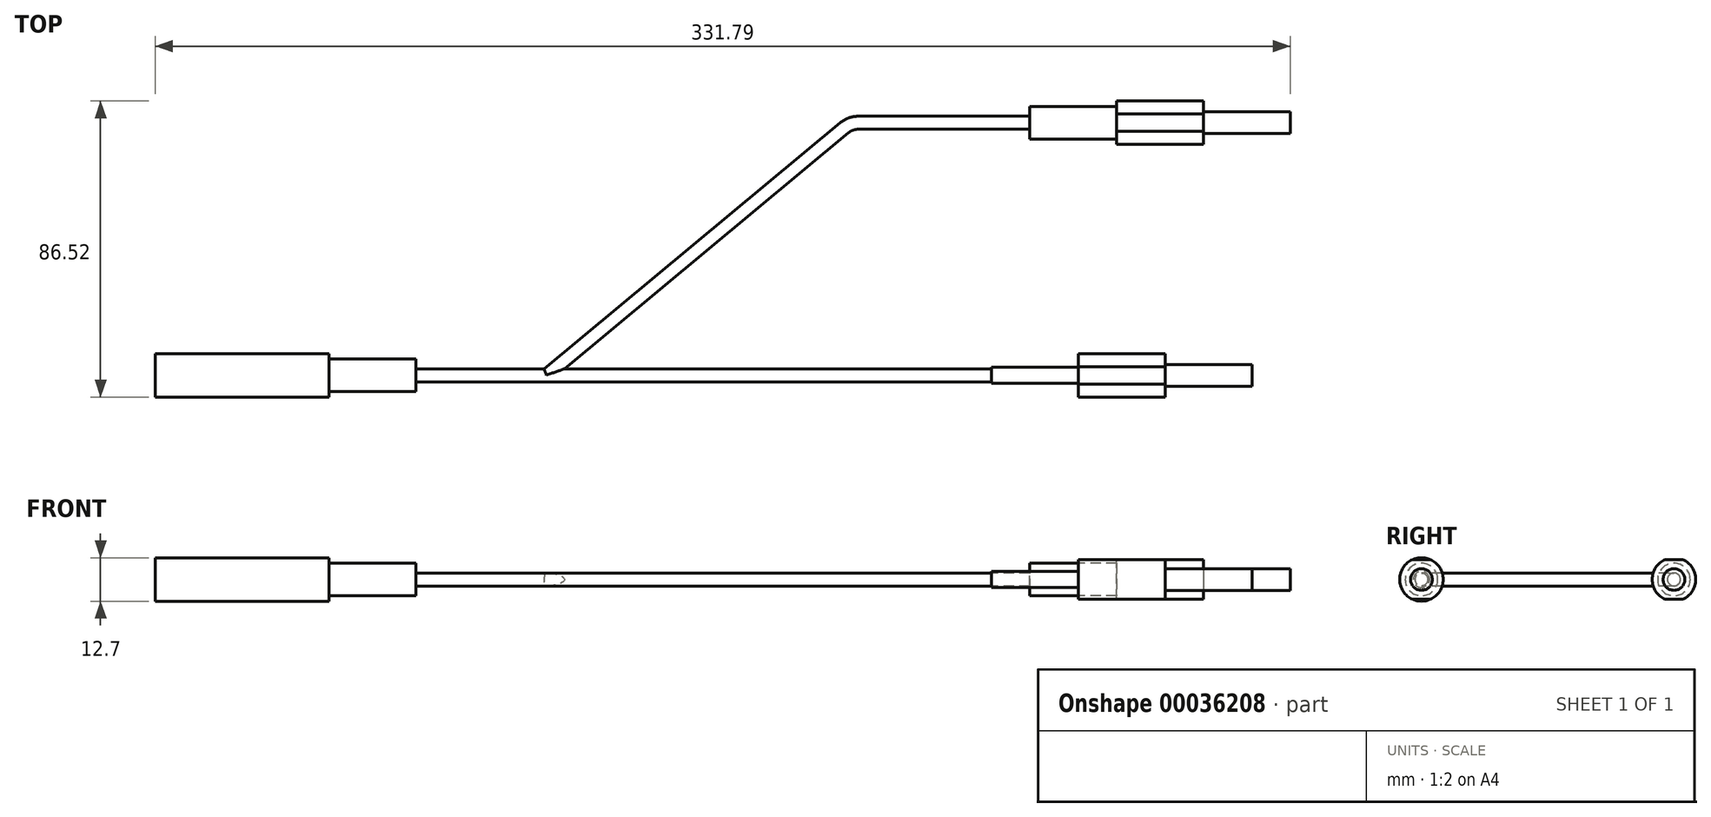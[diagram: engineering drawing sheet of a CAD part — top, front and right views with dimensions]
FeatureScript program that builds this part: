
annotation { "Feature Type Name" : "Feature", "Feature Type Description" : "" }
export const myFeature = defineFeature(function(context is Context, id is Id, definition is map)
    precondition{}
    {
        {
            var Q0;
            Q0=qCreatedBy(makeId("Top.planeOp"),FACE);
            var sketch = newSketch(context, id + "F0", { "sketchPlane" : qUnion([Q0])});
            skLineSegment(sketch, "E0", {"start": v(-154.29, 0) * mm, "end": v(235.8, 0) * mm, "construction": true});
            skLineSegment(sketch, "E1", {"start": v(-160.34, 0) * mm, "end": v(-160.34, -6.35) * mm});
            skLineSegment(sketch, "E2", {"start": v(-160.34, -6.35) * mm, "end": v(-109.54, -6.35) * mm});
            skLineSegment(sketch, "E3", {"start": v(160.34, 0) * mm, "end": v(160.34, -3.18) * mm});
            skLineSegment(sketch, "E4", {"start": v(-109.54, -6.35) * mm, "end": v(-109.54, -4.76) * mm});
            skLineSegment(sketch, "E5", {"start": v(-109.54, -4.76) * mm, "end": v(-84.14, -4.76) * mm});
            skLineSegment(sketch, "E6", {"start": v(-84.14, -4.76) * mm, "end": v(-84.14, -1.9) * mm});
            skLineSegment(sketch, "E7", {"start": v(-84.14, -1.9) * mm, "end": v(84.14, -1.9) * mm});
            skLineSegment(sketch, "E8", {"start": v(84.14, -1.9) * mm, "end": v(84.14, -2.38) * mm});
            skLineSegment(sketch, "E9", {"start": v(84.14, -2.38) * mm, "end": v(109.54, -2.38) * mm});
            skLineSegment(sketch, "E10", {"start": v(109.54, -6.35) * mm, "end": v(109.54, -2.38) * mm});
            skLineSegment(sketch, "E11", {"start": v(109.54, -6.35) * mm, "end": v(134.94, -6.35) * mm});
            skLineSegment(sketch, "E12", {"start": v(134.94, -6.35) * mm, "end": v(134.94, -3.18) * mm});
            skLineSegment(sketch, "E13", {"start": v(134.94, -3.18) * mm, "end": v(160.34, -3.18) * mm});
            skLineSegment(sketch, "E14", {"start": v(-160.34, 0) * mm, "end": v(160.34, 0) * mm});
            skLineSegment(sketch, "E15", {"start": v(-46.04, 0) * mm, "end": v(41.1, 72.35) * mm});
            skLineSegment(sketch, "E16", {"start": v(45.16, 73.82) * mm, "end": v(171.45, 73.82) * mm});
            skPoint(sketch, "E17.visualSharp", {"position": v(42.86, 73.82) * mm});
            skArc(sketch, "E17.filletArc", {"start": v(45.16, 73.82) * mm, "mid": v(43, 73.44) * mm, "end": v(41.1, 72.35) * mm});
            skSolve(sketch);
        }
        {
            var Q0;
            Q0=makeQuery(id+"F0.imprint","IMPRINT",FACE,{"disambiguationData":[TD([[makeQuery(id+"F0.imprint","IMPRINT",EDGE,{"derivedFrom":sQuery(id+"F0.wireOp",EDGE,"E1")}),1.0]])]});
            var Q1;
            Q1=sQuery(id+"F0.wireOp",EDGE,"E0");
            revolve(context, id + "F1", {"entities" : qUnion([Q0]), "axis" : qUnion([Q1]), "revolveType" : RevolveType.FULL});
        }
        {
            var Q0;
            Q0=qCreatedBy(makeId("Right.planeOp"),FACE);
            var Q1;
            Q1=sQuery(id+"F0.wireOp",VERTEX,"E16.end");
            cPlane(context, id + "F2", {"entities" : qUnion([Q0, Q1]), "cplaneType" : CPlaneType.PLANE_POINT, "offset" : 152.4 * mm, "width" : 152.4 * mm, "height" : 152.4 * mm});
        }
        {
            var Q0;
            Q0=qCreatedBy(id+"F2.planeOp",FACE);
            var sketch = newSketch(context, id + "F3", { "sketchPlane" : qUnion([Q0])});
            skCircle(sketch, "E18", {"center": v(73.82, 0) * mm, "radius": 1.9 * mm});
            skSolve(sketch);
        }
        {
            var Q0;
            Q0=makeQuery(id+"F3.imprint","IMPRINT",FACE,{"disambiguationData":[TD([[makeQuery(id+"F3.imprint","IMPRINT",EDGE,{"derivedFrom":sQuery(id+"F3.wireOp",EDGE,"E18")}),1.0]])]});
            var Q1;
            Q1=sQuery(id+"F0.wireOp",EDGE,"E16");
            var Q2;
            Q2=sQuery(id+"F0.wireOp",EDGE,"E17.filletArc");
            var Q3;
            Q3=sQuery(id+"F0.wireOp",EDGE,"E15");
            sweep(context, id + "F4", {"operationType" : NewBodyOperationType.ADD, "profiles" : qUnion([Q0]), "path" : qUnion([Q1, Q2, Q3])});
        }
        {
            var Q0;
            Q0=qCreatedBy(makeId("Top.planeOp"),FACE);
            var sketch = newSketch(context, id + "F5", { "sketchPlane" : qUnion([Q0])});
            skLineSegment(sketch, "E19", {"start": v(171.45, 73.82) * mm, "end": v(171.45, 77) * mm});
            skLineSegment(sketch, "E20", {"start": v(171.45, 77) * mm, "end": v(146.05, 77) * mm});
            skLineSegment(sketch, "E21", {"start": v(146.05, 80.17) * mm, "end": v(146.05, 77) * mm});
            skLineSegment(sketch, "E22", {"start": v(146.05, 80.17) * mm, "end": v(120.65, 80.17) * mm});
            skLineSegment(sketch, "E23", {"start": v(120.65, 80.17) * mm, "end": v(120.65, 78.58) * mm});
            skLineSegment(sketch, "E24", {"start": v(120.65, 78.58) * mm, "end": v(95.25, 78.58) * mm});
            skLineSegment(sketch, "E25", {"start": v(95.25, 78.58) * mm, "end": v(95.25, 73.82) * mm});
            skLineSegment(sketch, "E26", {"start": v(95.25, 73.82) * mm, "end": v(171.45, 73.82) * mm});
            skLineSegment(sketch, "E27", {"start": v(79.02, 73.82) * mm, "end": v(177.71, 73.82) * mm, "construction": true});
            skSolve(sketch);
        }
        {
            var Q0;
            Q0=makeQuery(id+"F5.imprint","IMPRINT",FACE,{"disambiguationData":[TD([[makeQuery(id+"F5.imprint","IMPRINT",EDGE,{"derivedFrom":sQuery(id+"F5.wireOp",EDGE,"E19")}),1.0]])]});
            var Q1;
            Q1=sQuery(id+"F5.wireOp",EDGE,"E27");
            revolve(context, id + "F6", {"operationType" : NewBodyOperationType.ADD, "entities" : qUnion([Q0]), "axis" : qUnion([Q1]), "revolveType" : RevolveType.FULL});
        }
        {
            var Q0;
            Q0=qCreatedBy(makeId("Right.planeOp"),FACE);
            var sketch = newSketch(context, id + "F7", { "sketchPlane" : qUnion([Q0])});
            skLineSegment(sketch, "E28.bottom", {"start": v(-2.54, 5.82) * mm, "end": v(76.36, 5.82) * mm});
            skLineSegment(sketch, "E28.top", {"start": v(-2.54, 6.35) * mm, "end": v(76.36, 6.35) * mm});
            skLineSegment(sketch, "E28.left", {"start": v(-2.54, 5.82) * mm, "end": v(-2.54, 6.35) * mm});
            skLineSegment(sketch, "E28.right", {"start": v(76.36, 5.82) * mm, "end": v(76.36, 6.35) * mm});
            skLineSegment(sketch, "E29.MirrorCS", {"start": v(76.36, -5.82) * mm, "end": v(76.36, -6.35) * mm});
            skLineSegment(sketch, "E30.MirrorCS", {"start": v(-2.54, -5.82) * mm, "end": v(-2.54, -6.35) * mm});
            skLineSegment(sketch, "E31.MirrorCS", {"start": v(-2.54, -5.82) * mm, "end": v(76.36, -5.82) * mm});
            skLineSegment(sketch, "E32.MirrorCS", {"start": v(-2.54, -6.35) * mm, "end": v(76.36, -6.35) * mm});
            skSolve(sketch);
        }
        {
            var Q0;
            Q0=makeQuery(id+"F7.imprint","IMPRINT",FACE,{"disambiguationData":[TD([[makeQuery(id+"F7.imprint","IMPRINT",EDGE,{"derivedFrom":sQuery(id+"F7.wireOp",EDGE,"E28.bottom")}),1.0]])]});
            var Q1;
            Q1=makeQuery(id+"F7.imprint","IMPRINT",FACE,{"disambiguationData":[TD([[makeQuery(id+"F7.imprint","IMPRINT",EDGE,{"derivedFrom":sQuery(id+"F7.wireOp",EDGE,"E29.MirrorCS")}),-1.0]])]});
            extrude(context, id + "F8", {"entities" : qUnion([Q0, Q1]), "operationType" : NewBodyOperationType.REMOVE, "endBound" : BoundingType.THROUGH_ALL, "depth" : 25.4 * mm});
        }
    });
